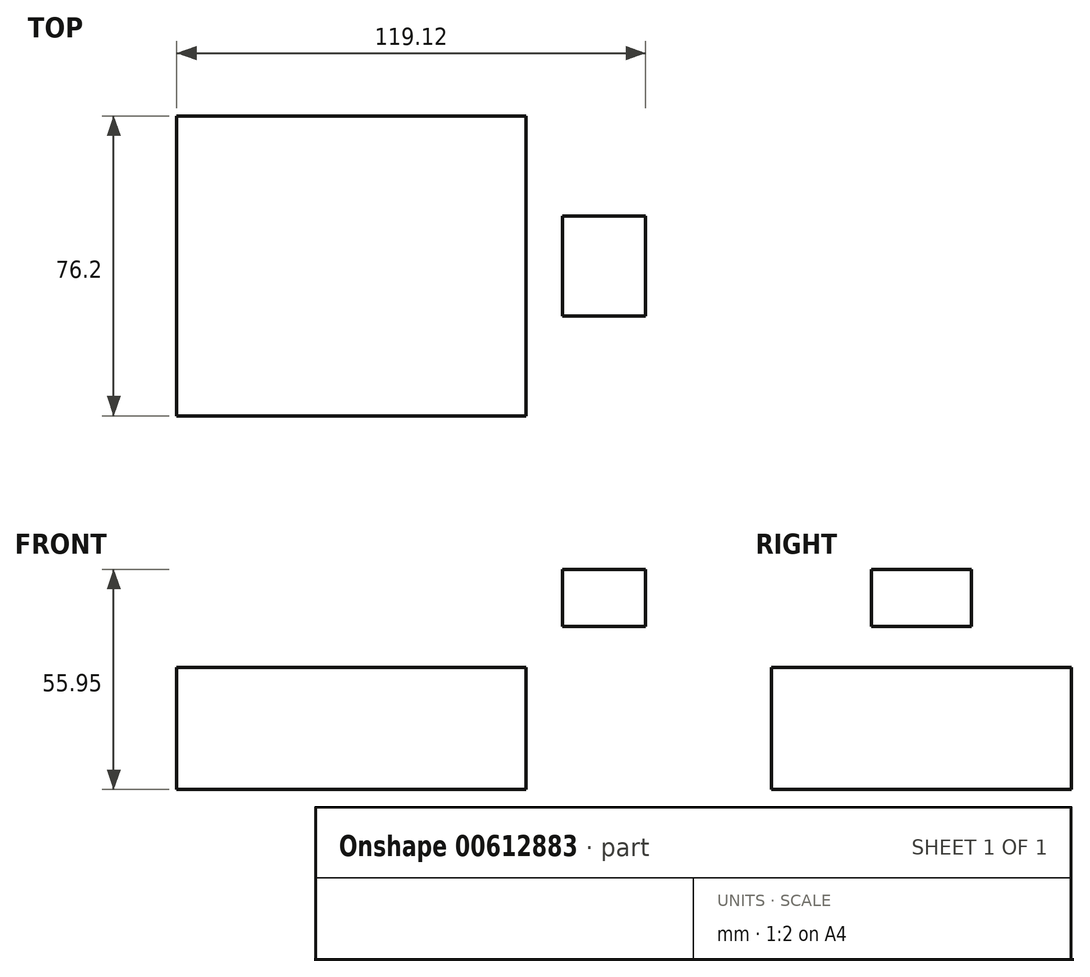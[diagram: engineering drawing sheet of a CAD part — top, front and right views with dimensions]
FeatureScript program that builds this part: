
annotation { "Feature Type Name" : "Feature", "Feature Type Description" : "" }
export const myFeature = defineFeature(function(context is Context, id is Id, definition is map)
    precondition{}
    {
        {
            var Q0;
            Q0=qCreatedBy(makeId("Front.planeOp"),FACE);
            var sketch = newSketch(context, id + "F0", { "sketchPlane" : qUnion([Q0])});
            skLineSegment(sketch, "E0.bottom", {"start": v(44.37, 15.5) * mm, "end": v(-44.37, 15.5) * mm});
            skLineSegment(sketch, "E0.top", {"start": v(44.37, -15.5) * mm, "end": v(-44.37, -15.5) * mm});
            skLineSegment(sketch, "E0.left", {"start": v(44.37, 15.5) * mm, "end": v(44.37, -15.5) * mm});
            skLineSegment(sketch, "E0.right", {"start": v(-44.37, 15.5) * mm, "end": v(-44.37, -15.5) * mm});
            skPoint(sketch, "E0.middle", {"position": v(0, 0) * mm});
            skSolve(sketch);
        }
        {
            var Q0;
            Q0=qCreatedBy(makeId("Front.planeOp"),FACE);
            var sketch = newSketch(context, id + "F1", { "sketchPlane" : qUnion([Q0])});
            skLineSegment(sketch, "E1.bottom", {"start": v(74.75, 40.46) * mm, "end": v(53.7, 40.46) * mm});
            skLineSegment(sketch, "E1.top", {"start": v(74.75, 26.02) * mm, "end": v(53.7, 26.02) * mm});
            skLineSegment(sketch, "E1.left", {"start": v(74.75, 40.46) * mm, "end": v(74.75, 26.02) * mm});
            skLineSegment(sketch, "E1.right", {"start": v(53.7, 40.46) * mm, "end": v(53.7, 26.02) * mm});
            skPoint(sketch, "E1.middle", {"position": v(64.22, 33.24) * mm});
            skLineSegment(sketch, "E2", {"start": v(44.07, 15.74) * mm, "end": v(44.07, 22.76) * mm});
            skSolve(sketch);
        }
        {
            var Q0;
            Q0=makeQuery(id+"F0.imprint","IMPRINT",FACE,{"disambiguationData":[TD([[makeQuery(id+"F0.imprint","IMPRINT",EDGE,{"derivedFrom":sQuery(id+"F0.wireOp",EDGE,"E0.bottom")}),1.0]])]});
            extrude(context, id + "F2", {"entities" : qUnion([Q0]), "endBound" : BoundingType.SYMMETRIC, "depth" : 76.2 * mm, "offsetDistance" : 25.4 * mm, "hasSecondDirection" : true, "secondDirectionOppositeDirection" : true, "secondDirectionDepth" : 25.4 * mm});
        }
        {
            var Q0;
            Q0=makeQuery(id+"F1.imprint","IMPRINT",FACE,{"disambiguationData":[TD([[makeQuery(id+"F1.imprint","IMPRINT",EDGE,{"derivedFrom":sQuery(id+"F1.wireOp",EDGE,"E1.bottom")}),1.0]])]});
            extrude(context, id + "F3", {"entities" : qUnion([Q0]), "endBound" : BoundingType.SYMMETRIC, "depth" : 25.4 * mm, "offsetDistance" : 25.4 * mm});
        }
    });
